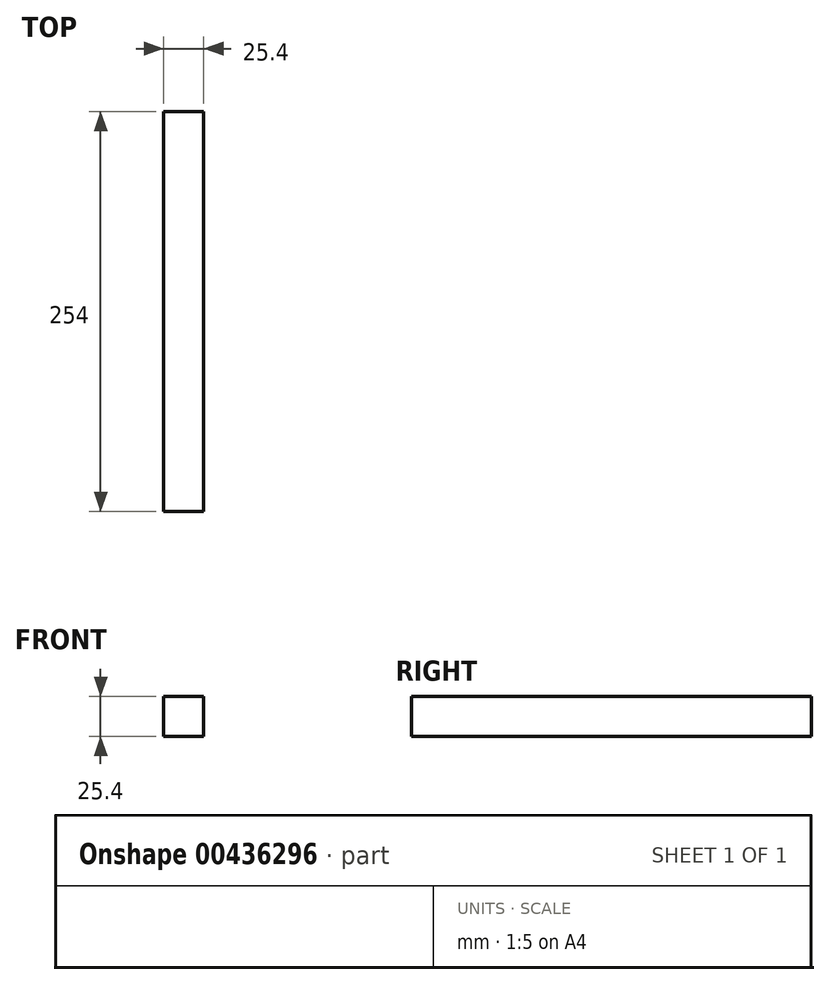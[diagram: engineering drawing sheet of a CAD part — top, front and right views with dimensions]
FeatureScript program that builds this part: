
annotation { "Feature Type Name" : "Feature", "Feature Type Description" : "" }
export const myFeature = defineFeature(function(context is Context, id is Id, definition is map)
    precondition{}
    {
        {
            var Q0;
            Q0=qCreatedBy(makeId("Front.planeOp"),FACE);
            var sketch = newSketch(context, id + "F0", { "sketchPlane" : qUnion([Q0])});
            skLineSegment(sketch, "E0.bottom", {"start": v(0, 0) * mm, "end": v(25.4, 0) * mm});
            skLineSegment(sketch, "E0.top", {"start": v(0, 25.4) * mm, "end": v(25.4, 25.4) * mm});
            skLineSegment(sketch, "E0.left", {"start": v(0, 0) * mm, "end": v(0, 25.4) * mm});
            skLineSegment(sketch, "E0.right", {"start": v(25.4, 0) * mm, "end": v(25.4, 25.4) * mm});
            skSolve(sketch);
        }
        {
            var Q0;
            Q0 = qSketchRegion(id + "F0", true);
            extrude(context, id + "F1", {"entities" : qUnion([Q0]), "depth" : 254 * mm});
        }
    });
